# Revit family: 603-A-6100-DN40-200
name_source: partatom
category: Pipe Accessories
units: mm (PartAtom-declared; Revit-internal decimal feet)

## family parameters
Always vertical = Yes
Cut with Voids When Loaded = No
Part Type = Valve - Breaks Into
Round Connector Dimension = Use Diameter
Shared = No
Work Plane-Based = No

## types (14) — shared parameters
Bolt_width = 20 mm  [stored 0.0656168 ft]
DN040/50_ 46 - 63 = 603-063-000-6100
DN050/65_57 - 74 = 603-074-001-6100
DN050_57 - 74 = 603-074-000-6100
DN080/100_84 - 106 = 603-106-001-6100
DN080_84 - 106 = 603-106-000-6100
DN100/125_109 - 133 = 603-133-001-6100
DN100_109 - 133 = 603-133-000-6100
DN100_99 - 119 = 603-119-000-6100
DN125/150_132 - 157 = 603-157-000-6100
DN150_ 157 -183 = 603-183-000-6100
DN150_176 - 201 = 603-201-000-6100
DN200_193 - 215 = 603-215-000-6100
DN200_218 - 242 = 603-242-000-6100
Nut = 10 mm  [stored 0.0328084 ft]
Rib_Thickness = 5 mm  [stored 0.0164042 ft]
Rib_length = 32 mm  [stored 0.104987 ft]
Search_table = 603-A-6100-DN40-200
URL product pages = https://www.avkvalves.com
Washer = 3 mm  [stored 0.00984252 ft]

## per-type parameters (varying)
- 603-063-000-4100_DN040/50: Bolt_ref=119 mm; Bottm_cut=28 mm; Bottm_height=7 mm  [stored 0.0229659 ft]; Bottom_Flange_Thicckness=19 mm  [stored 0.062336 ft]; Bottom_Flange_Thicckness_2=10 mm  [stored 0.0328084 ft]; D=83 mm; D2=38 mm; D3=45 mm  [stored 0.147638 ft]; D4=69 mm  [stored 0.226378 ft]; DN050/65_ 68 - 85=603-085-000-6100; DN1=32 mm  [stored 0.104987 ft]; DN1_ref=63 mm  [stored 0.206693 ft]; DN2=23 mm  [stored 0.0754593 ft]; DN2_ref=46 mm  [stored 0.150919 ft]; Description_=AVK UNIVERSAL SUPA® FLANGE ADAPTOR; H1=32 mm  [stored 0.104987 ft]; ID=20 mm  [stored 0.0656168 ft]; L=164 mm; L1=47 mm  [stored 0.154199 ft]; L2=145 mm; L3=79 mm; Length=99 mm; Nomianal_Diameter(DN)=40 mm  [stored 0.131234 ft]; PCD=100 mm; Rib_width=130 mm; Washer_ref=109 mm
- 603-074-001-4100_DN050/60/65: Bolt_ref=119 mm; Bottm_cut=49 mm  [stored 0.160761 ft]; Bottm_height=7 mm  [stored 0.0229659 ft]; Bottom_Flange_Thicckness=19 mm  [stored 0.062336 ft]; Bottom_Flange_Thicckness_2=10 mm  [stored 0.0328084 ft]; D=93 mm; D2=47 mm  [stored 0.154199 ft]; D3=56 mm  [stored 0.183727 ft]; D4=87 mm; DN050/65_ 68 - 85=603-085-000-6100; DN1=37 mm  [stored 0.121391 ft]; DN1_ref=74 mm; DN2=29 mm; DN2_ref=57 mm  [stored 0.187008 ft]; Description_=AVK UNIVERSAL SUPA® FLANGE ADAPTOR
AVK UNIVERSAL SUPA® FLANGE ADAPTOR; H1=32 mm  [stored 0.104987 ft]; ID=25 mm  [stored 0.082021 ft]; L=164 mm; L1=47 mm  [stored 0.154199 ft]; L2=145 mm; L3=79 mm; Length=99 mm; Nomianal_Diameter(DN)=50 mm  [stored 0.164042 ft]; PCD=136 mm; Rib_width=174 mm; Washer_ref=109 mm
- 603-074-000-4100_DN050: Bolt_ref=119 mm; Bottm_cut=49 mm  [stored 0.160761 ft]; Bottm_height=7 mm  [stored 0.0229659 ft]; Bottom_Flange_Thicckness=19 mm  [stored 0.062336 ft]; Bottom_Flange_Thicckness_2=10 mm  [stored 0.0328084 ft]; D=86 mm; D2=47 mm  [stored 0.154199 ft]; D3=56 mm  [stored 0.183727 ft]; D4=87 mm; DN050/65_ 68 - 85=603-085-000-6100; DN1=37 mm  [stored 0.121391 ft]; DN1_ref=74 mm; DN2=29 mm; DN2_ref=57 mm  [stored 0.187008 ft]; Description_=AVK UNIVERSAL SUPA® FLANGE ADAPTOR; H1=32 mm  [stored 0.104987 ft]; ID=25 mm  [stored 0.082021 ft]; L=164 mm; L1=47 mm  [stored 0.154199 ft]; L2=145 mm; L3=79 mm; Length=99 mm; Nomianal_Diameter(DN)=50 mm  [stored 0.164042 ft]; PCD=136 mm; Rib_width=174 mm; Washer_ref=109 mm
- 603-085-000-4100_DN050/60/65: Bolt_ref=119 mm; Bottm_cut=49 mm  [stored 0.160761 ft]; Bottm_height=7 mm  [stored 0.0229659 ft]; Bottom_Flange_Thicckness=19 mm  [stored 0.062336 ft]; Bottom_Flange_Thicckness_2=10 mm  [stored 0.0328084 ft]; D=93 mm; D2=50 mm  [stored 0.164042 ft]; D3=60 mm; D4=87 mm; DN050/65_ 68 - 85=603-085-000-6100; DN1=43 mm; DN1_ref=85 mm; DN2=34 mm  [stored 0.111549 ft]; DN2_ref=68 mm  [stored 0.223097 ft]; Description_=AVK UNIVERSAL SUPA® FLANGE ADAPTOR; H1=32 mm  [stored 0.104987 ft]; ID=33 mm  [stored 0.108268 ft]; L=164 mm; L1=47 mm  [stored 0.154199 ft]; L2=145 mm; L3=79 mm; Length=99 mm; Nomianal_Diameter(DN)=65 mm; PCD=136 mm; Rib_width=174 mm; Washer_ref=109 mm
- 603-106-001-4100_DN080/100: Bolt_ref=122 mm; Bottm_cut=67 mm; Bottm_height=7 mm  [stored 0.0229659 ft]; Bottom_Flange_Thicckness=19 mm  [stored 0.062336 ft]; Bottom_Flange_Thicckness_2=10 mm  [stored 0.0328084 ft]; D=115 mm; D2=63 mm  [stored 0.206693 ft]; D3=76 mm; D4=102 mm; DN050/65_ 68 - 85=603-085-000-6100; DN1=53 mm  [stored 0.173885 ft]; DN1_ref=106 mm; DN2=42 mm  [stored 0.137795 ft]; DN2_ref=84 mm; Description_=AVK UNIVERSAL SUPA® FLANGE ADAPTOR; H1=33 mm  [stored 0.108268 ft]; ID=40 mm  [stored 0.131234 ft]; L=164 mm; L1=47 mm  [stored 0.154199 ft]; L2=145 mm; L3=81 mm; Length=100 mm; Nomianal_Diameter(DN)=80 mm; PCD=165 mm; Rib_width=213 mm; Washer_ref=112 mm
- 603-106-000-4100_DN080: Bolt_ref=127 mm; Bottm_cut=67 mm; Bottm_height=7 mm  [stored 0.0229659 ft]; Bottom_Flange_Thicckness=14 mm  [stored 0.0459318 ft]; Bottom_Flange_Thicckness_2=7 mm  [stored 0.0229659 ft]; D=100 mm; D2=63 mm  [stored 0.206693 ft]; D3=76 mm; D4=97 mm; DN050/65_ 68 - 85=603-085-000-6100; DN1=53 mm  [stored 0.173885 ft]; DN1_ref=106 mm; DN2=42 mm  [stored 0.137795 ft]; DN2_ref=84 mm; Description_=AVK UNIVERSAL SUPA® FLANGE ADAPTOR; H1=33 mm  [stored 0.108268 ft]; ID=40 mm  [stored 0.131234 ft]; L=159 mm; L1=47 mm  [stored 0.154199 ft]; L2=145 mm; L3=86 mm; Length=99 mm; Nomianal_Diameter(DN)=80 mm; PCD=165 mm; Rib_width=213 mm; Washer_ref=117 mm
- 603-119-000-4100_DN100: Bolt_ref=127 mm; Bottm_cut=77 mm; Bottm_height=7 mm  [stored 0.0229659 ft]; Bottom_Flange_Thicckness=14 mm  [stored 0.0459318 ft]; Bottom_Flange_Thicckness_2=7 mm  [stored 0.0229659 ft]; D=115 mm; D2=69 mm  [stored 0.226378 ft]; D3=83 mm; D4=107 mm; DN050/65_ 68 - 85=603-085-001-6100; DN1=60 mm; DN1_ref=119 mm; DN2=50 mm  [stored 0.164042 ft]; DN2_ref=99 mm; Description_=AVK UNIVERSAL SUPA® FLANGE ADAPTOR; H1=33 mm  [stored 0.108268 ft]; ID=50 mm  [stored 0.164042 ft]; L=159 mm; L1=47 mm  [stored 0.154199 ft]; L2=145 mm; L3=86 mm; Length=99 mm; Nomianal_Diameter(DN)=100 mm; PCD=185 mm; Rib_width=226 mm; Washer_ref=117 mm
- 603-133-000-4100_DN100: Bolt_ref=127 mm; Bottm_cut=77 mm; Bottm_height=7 mm  [stored 0.0229659 ft]; Bottom_Flange_Thicckness=14 mm  [stored 0.0459318 ft]; Bottom_Flange_Thicckness_2=7 mm  [stored 0.0229659 ft]; D=115 mm; D2=75 mm; D3=90 mm; D4=107 mm; DN050/65_ 68 - 85=603-085-000-6100; DN1=67 mm; DN1_ref=133 mm; DN2=55 mm  [stored 0.180446 ft]; DN2_ref=109 mm; Description_=AVK UNIVERSAL SUPA® FLANGE ADAPTOR; H1=33 mm  [stored 0.108268 ft]; ID=50 mm  [stored 0.164042 ft]; L=159 mm; L1=47 mm  [stored 0.154199 ft]; L2=145 mm; L3=87 mm; Length=159 mm; Nomianal_Diameter(DN)=100 mm; PCD=185 mm; Rib_width=226 mm; Washer_ref=117 mm
- 603-133-001-4100_DN100/125: Bolt_ref=123 mm; Bottm_cut=77 mm; Bottm_height=7 mm  [stored 0.0229659 ft]; Bottom_Flange_Thicckness=19 mm  [stored 0.062336 ft]; Bottom_Flange_Thicckness_2=10 mm  [stored 0.0328084 ft]; D=127 mm; D2=75 mm; D3=90 mm; D4=112 mm; DN050/65_ 68 - 85=603-085-000-6100; DN1=67 mm; DN1_ref=133 mm; DN2=55 mm  [stored 0.180446 ft]; DN2_ref=109 mm; Description_=AVK UNIVERSAL SUPA® FLANGE ADAPTOR; H1=33 mm  [stored 0.108268 ft]; ID=50 mm  [stored 0.164042 ft]; L=164 mm; L1=47 mm  [stored 0.154199 ft]; L2=145 mm; L3=82 mm; Length=99 mm; Nomianal_Diameter(DN)=100 mm; PCD=185 mm; Rib_width=226 mm; Washer_ref=113 mm
- 603-157-000-4100_DN125/150: Bolt_ref=139 mm; Bottm_cut=88 mm; Bottm_height=7 mm  [stored 0.0229659 ft]; Bottom_Flange_Thicckness=14 mm  [stored 0.0459318 ft]; Bottom_Flange_Thicckness_2=7 mm  [stored 0.0229659 ft]; D=143 mm; D2=89 mm; D3=106 mm; D4=129 mm; DN050/65_ 68 - 85=603-085-000-6100; DN1=79 mm; DN1_ref=157 mm; DN2=66 mm  [stored 0.216535 ft]; DN2_ref=132 mm; Description_=AVK UNIVERSAL SUPA® FLANGE ADAPTOR; H1=34 mm  [stored 0.111549 ft]; ID=63 mm  [stored 0.206693 ft]; L=184 mm; L1=58 mm  [stored 0.190289 ft]; L2=170 mm; L3=97 mm; Length=116 mm; Nomianal_Diameter(DN)=125 mm; PCD=230 mm; Rib_width=270 mm; Washer_ref=129 mm
- 603-183-000-4100_DN150: Bolt_ref=138 mm; Bottm_cut=105 mm; Bottm_height=7 mm  [stored 0.0229659 ft]; Bottom_Flange_Thicckness=14 mm  [stored 0.0459318 ft]; Bottom_Flange_Thicckness_2=7 mm  [stored 0.0229659 ft]; D=143 mm; D2=105 mm; D3=126 mm; D4=139 mm; DN050/65_ 68 - 85=603-085-000-6100; DN1=92 mm; DN1_ref=183 mm; DN2=79 mm; DN2_ref=157 mm; Description_=AVK UNIVERSAL SUPA® FLANGE ADAPTOR; H1=35 mm  [stored 0.114829 ft]; ID=75 mm; L=184 mm; L1=52 mm; L2=170 mm; L3=95 mm; Length=116 mm; Nomianal_Diameter(DN)=150 mm; PCD=250 mm; Rib_width=298 mm; Washer_ref=128 mm
- 603-201-000-4100_DN150: Bolt_ref=141 mm; Bottm_cut=105 mm; Bottm_height=7 mm  [stored 0.0229659 ft]; Bottom_Flange_Thicckness=14 mm  [stored 0.0459318 ft]; Bottom_Flange_Thicckness_2=7 mm  [stored 0.0229659 ft]; D=143 mm; D2=105 mm; D3=126 mm; D4=144 mm; DN050/65_ 68 - 85=603-085-000-6100; DN1=101 mm; DN1_ref=201 mm; DN2=88 mm; DN2_ref=176 mm; Description_=AVK UNIVERSAL SUPA® FLANGE ADAPTOR; H1=35 mm  [stored 0.114829 ft]; ID=75 mm; L=184 mm; L1=53 mm  [stored 0.173885 ft]; L2=170 mm; L3=98 mm; Length=116 mm; Nomianal_Diameter(DN)=150 mm; PCD=260 mm; Rib_width=298 mm; Washer_ref=131 mm
- 603-215-000-4100_DN200: Bolt_ref=148 mm; Bottm_cut=132 mm; Bottm_height=5 mm  [stored 0.0164042 ft]; Bottom_Flange_Thicckness=12 mm  [stored 0.0393701 ft]; Bottom_Flange_Thicckness_2=6 mm  [stored 0.019685 ft]; D=172 mm; D2=120 mm; D3=143 mm; D4=162 mm; DN050/65_ 68 - 85=603-085-000-6100; DN1=108 mm; DN1_ref=215 mm; DN2=97 mm; DN2_ref=193 mm; Description_=AVK UNIVERSAL SUPA® FLANGE ADAPTOR; H1=35 mm  [stored 0.114829 ft]; ID=100 mm; L=182 mm; L1=53 mm  [stored 0.173885 ft]; L2=170 mm; L3=105 mm; Length=117 mm; Nomianal_Diameter(DN)=200 mm; PCD=300 mm; Rib_width=326 mm; Washer_ref=138 mm
- 603-242-000-4100_DN200: Bolt_ref=148 mm; Bottm_cut=132 mm; Bottm_height=5 mm  [stored 0.0164042 ft]; Bottom_Flange_Thicckness=12 mm  [stored 0.0393701 ft]; Bottom_Flange_Thicckness_2=6 mm  [stored 0.019685 ft]; D=172 mm; D2=130 mm; D3=141 mm; D4=162 mm; DN050/65_ 68 - 85=603-085-000-6100; DN1=121 mm; DN1_ref=242 mm; DN2=109 mm; DN2_ref=218 mm; Description_=AVK UNIVERSAL SUPA® FLANGE ADAPTOR; H1=35 mm  [stored 0.114829 ft]; ID=100 mm; L=182 mm; L1=53 mm  [stored 0.173885 ft]; L2=170 mm; L3=105 mm; Length=117 mm; Nomianal_Diameter(DN)=200 mm; PCD=300 mm; Rib_width=326 mm; Washer_ref=138 mm

note: [stored X ft] marks values corroborated as IEEE doubles in the binary element streams (Revit-internal decimal feet)

## geometry (parser evidence)
native form markers: Sweep x16
no freeform markers — native parametric forms only
